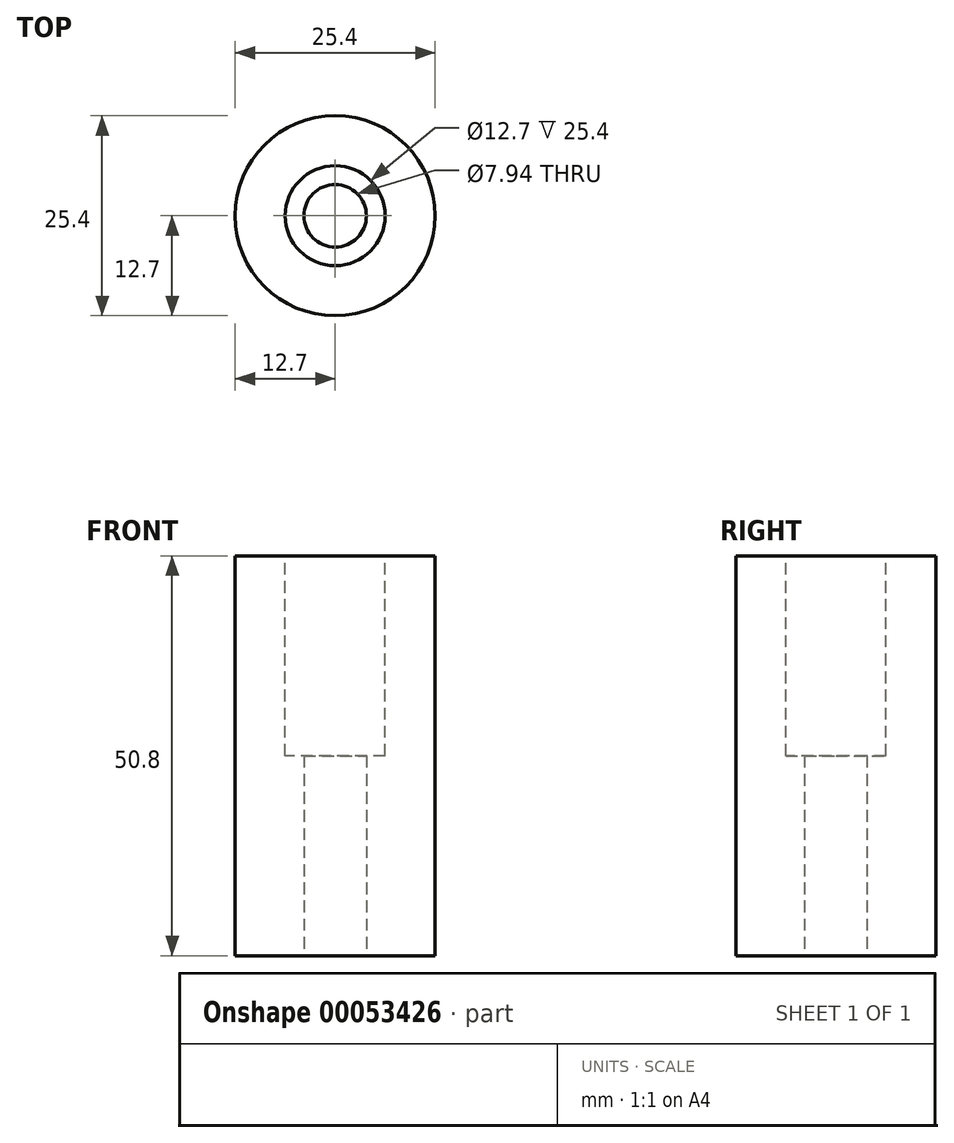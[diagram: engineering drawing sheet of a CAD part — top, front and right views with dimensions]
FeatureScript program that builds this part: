
annotation { "Feature Type Name" : "Feature", "Feature Type Description" : "" }
export const myFeature = defineFeature(function(context is Context, id is Id, definition is map)
    precondition{}
    {
        {
            var Q0;
            Q0=qCreatedBy(makeId("Top.planeOp"),FACE);
            var sketch = newSketch(context, id + "F0", { "sketchPlane" : qUnion([Q0])});
            skCircle(sketch, "E0", {"center": v(0, 0) * mm, "radius": 12.7 * mm});
            skSolve(sketch);
        }
        {
            var Q0;
            Q0 = qSketchRegion(id + "F0", true);
            extrude(context, id + "F1", {"entities" : qUnion([Q0]), "depth" : 50.8 * mm});
        }
        {
            var Q0;
            Q0 = qSketchRegion(id + "F0", true);
            extrude(context, id + "F2", {"entities" : qUnion([Q0]), "operationType" : NewBodyOperationType.ADD, "depth" : 50.8 * mm});
        }
        {
            var Q0;
            Q0=makeQuery(id+"F1.opExtrude","CAP_FACE",FACE,{"disambiguationData":[OSD([sQuery(id+"F0.wireOp",EDGE,"E0")])],"isStart":false});
            var sketch = newSketch(context, id + "F3", { "sketchPlane" : qUnion([Q0])});
            skCircle(sketch, "E1", {"center": v(0, 0) * mm, "radius": 6.35 * mm});
            skSolve(sketch);
        }
        {
            var Q0;
            Q0 = qSketchRegion(id + "F3", true);
            extrude(context, id + "F4", {"entities" : qUnion([Q0]), "operationType" : NewBodyOperationType.REMOVE, "oppositeDirection" : true, "depth" : 25.4 * mm});
        }
        {
            var Q0;
            Q0=makeQuery(id+"F1.opExtrude","CAP_FACE",FACE,{"disambiguationData":[OSD([sQuery(id+"F0.wireOp",EDGE,"E0")])],"isStart":true});
            var sketch = newSketch(context, id + "F5", { "sketchPlane" : qUnion([Q0])});
            skCircle(sketch, "E2", {"center": v(0, 0) * mm, "radius": 3.97 * mm});
            skSolve(sketch);
        }
        {
            var Q0;
            Q0 = qSketchRegion(id + "F5", true);
            extrude(context, id + "F6", {"entities" : qUnion([Q0]), "operationType" : NewBodyOperationType.REMOVE, "oppositeDirection" : true, "depth" : 25.4 * mm});
        }
    });
